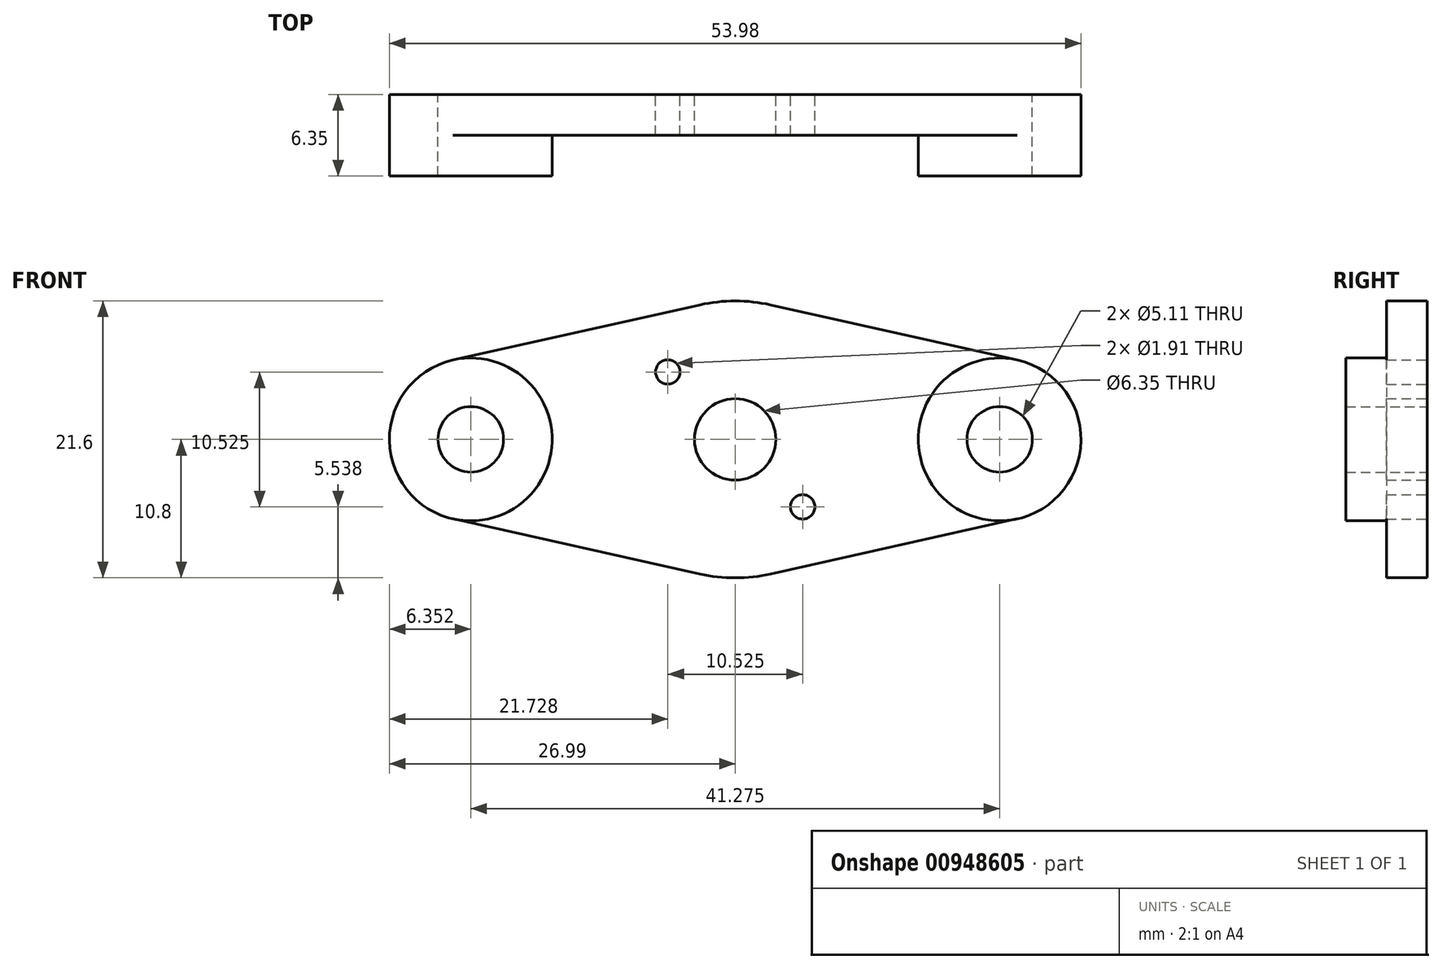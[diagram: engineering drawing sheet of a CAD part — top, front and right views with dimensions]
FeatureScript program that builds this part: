
annotation { "Feature Type Name" : "Feature", "Feature Type Description" : "" }
export const myFeature = defineFeature(function(context is Context, id is Id, definition is map)
    precondition{}
    {
        {
            var Q0;
            Q0=qCreatedBy(makeId("Front.planeOp"),FACE);
            var sketch = newSketch(context, id + "F0", { "sketchPlane" : qUnion([Q0])});
            skCircle(sketch, "E0", {"center": v(-20.64, 0) * mm, "radius": 2.55 * mm});
            skCircle(sketch, "E1", {"center": v(20.64, 0) * mm, "radius": 2.55 * mm});
            skLineSegment(sketch, "E2", {"start": v(20.64, 0) * mm, "end": v(0, 0) * mm, "construction": true});
            skLineSegment(sketch, "E3", {"start": v(-20.64, 0) * mm, "end": v(0, 0) * mm, "construction": true});
            skPoint(sketch, "E4.middle", {"position": v(0, 0) * mm});
            skCircle(sketch, "E5", {"center": v(0, 0) * mm, "radius": 3.18 * mm});
            skLineSegment(sketch, "E6", {"start": v(5.26, -5.26) * mm, "end": v(0, 0) * mm, "construction": true});
            skLineSegment(sketch, "E7", {"start": v(0, 0) * mm, "end": v(-5.26, 5.26) * mm, "construction": true});
            skCircle(sketch, "E8", {"center": v(-5.26, 5.26) * mm, "radius": 0.95 * mm});
            skCircle(sketch, "E9", {"center": v(5.26, -5.26) * mm, "radius": 0.95 * mm});
            skArc(sketch, "E10", {"start": v(-22.02, 6.2) * mm, "mid": v(-26.99, 0) * mm, "end": v(-22.02, -6.2) * mm});
            skLineSegment(sketch, "E11", {"start": v(-22.02, -6.2) * mm, "end": v(-2.77, -10.5) * mm});
            skLineSegment(sketch, "E12", {"start": v(2.77, -10.5) * mm, "end": v(22.02, -6.2) * mm});
            skArc(sketch, "E13", {"start": v(22.02, -6.2) * mm, "mid": v(26.99, 0) * mm, "end": v(22.02, 6.2) * mm});
            skLineSegment(sketch, "E14", {"start": v(22.02, 6.2) * mm, "end": v(2.77, 10.5) * mm});
            skLineSegment(sketch, "E15", {"start": v(-2.77, 10.5) * mm, "end": v(-22.02, 6.2) * mm});
            skCircle(sketch, "E16", {"center": v(-20.64, 0) * mm, "radius": 6.35 * mm, "construction": true});
            skCircle(sketch, "E17", {"center": v(20.64, 0) * mm, "radius": 6.35 * mm, "construction": true});
            skPoint(sketch, "E18.visualSharp", {"position": v(0, 11.11) * mm});
            skArc(sketch, "E18.filletArc", {"start": v(2.77, 10.5) * mm, "mid": v(0, 10.8) * mm, "end": v(-2.77, 10.5) * mm});
            skPoint(sketch, "E19.visualSharp", {"position": v(0, -11.11) * mm});
            skArc(sketch, "E19.filletArc", {"start": v(-2.77, -10.5) * mm, "mid": v(0, -10.8) * mm, "end": v(2.77, -10.5) * mm});
            skSolve(sketch);
        }
        {
            var Q0;
            Q0=makeQuery(id+"F0.imprint","IMPRINT",FACE,{"disambiguationData":[TD([[makeQuery(id+"F0.imprint","IMPRINT",EDGE,{"derivedFrom":sQuery(id+"F0.wireOp",EDGE,"E0")}),-1.0]])]});
            extrude(context, id + "F1", {"entities" : qUnion([Q0]), "depth" : 3.17 * mm, "offsetDistance" : 25.4 * mm});
        }
        {
            var Q0;
            Q0=makeQuery(id+"F1.opExtrude","CAP_FACE",FACE,{"disambiguationData":[OSD([sQuery(id+"F0.wireOp",EDGE,"E0"),sQuery(id+"F0.wireOp",EDGE,"E1"),sQuery(id+"F0.wireOp",EDGE,"E5"),sQuery(id+"F0.wireOp",EDGE,"E8"),sQuery(id+"F0.wireOp",EDGE,"E9"),sQuery(id+"F0.wireOp",EDGE,"E10"),sQuery(id+"F0.wireOp",EDGE,"E11"),sQuery(id+"F0.wireOp",EDGE,"E12"),sQuery(id+"F0.wireOp",EDGE,"E13"),sQuery(id+"F0.wireOp",EDGE,"E14"),sQuery(id+"F0.wireOp",EDGE,"E15"),sQuery(id+"F0.wireOp",EDGE,"E18.filletArc"),sQuery(id+"F0.wireOp",EDGE,"E19.filletArc")])],"isStart":false});
            var sketch = newSketch(context, id + "F2", { "sketchPlane" : qUnion([Q0])});
            skCircle(sketch, "E20", {"center": v(-20.64, 0) * mm, "radius": 2.55 * mm});
            skCircle(sketch, "E21", {"center": v(20.64, 0) * mm, "radius": 2.55 * mm});
            skCircle(sketch, "E22", {"center": v(20.64, 0) * mm, "radius": 6.35 * mm});
            skCircle(sketch, "E23", {"center": v(-20.64, 0) * mm, "radius": 6.35 * mm});
            skSolve(sketch);
        }
        {
            var Q0;
            Q0 = qSketchRegion(id + "F2", true);
            extrude(context, id + "F3", {"entities" : qUnion([Q0]), "operationType" : NewBodyOperationType.ADD, "depth" : 3.17 * mm, "offsetDistance" : 25.4 * mm});
        }
    });
